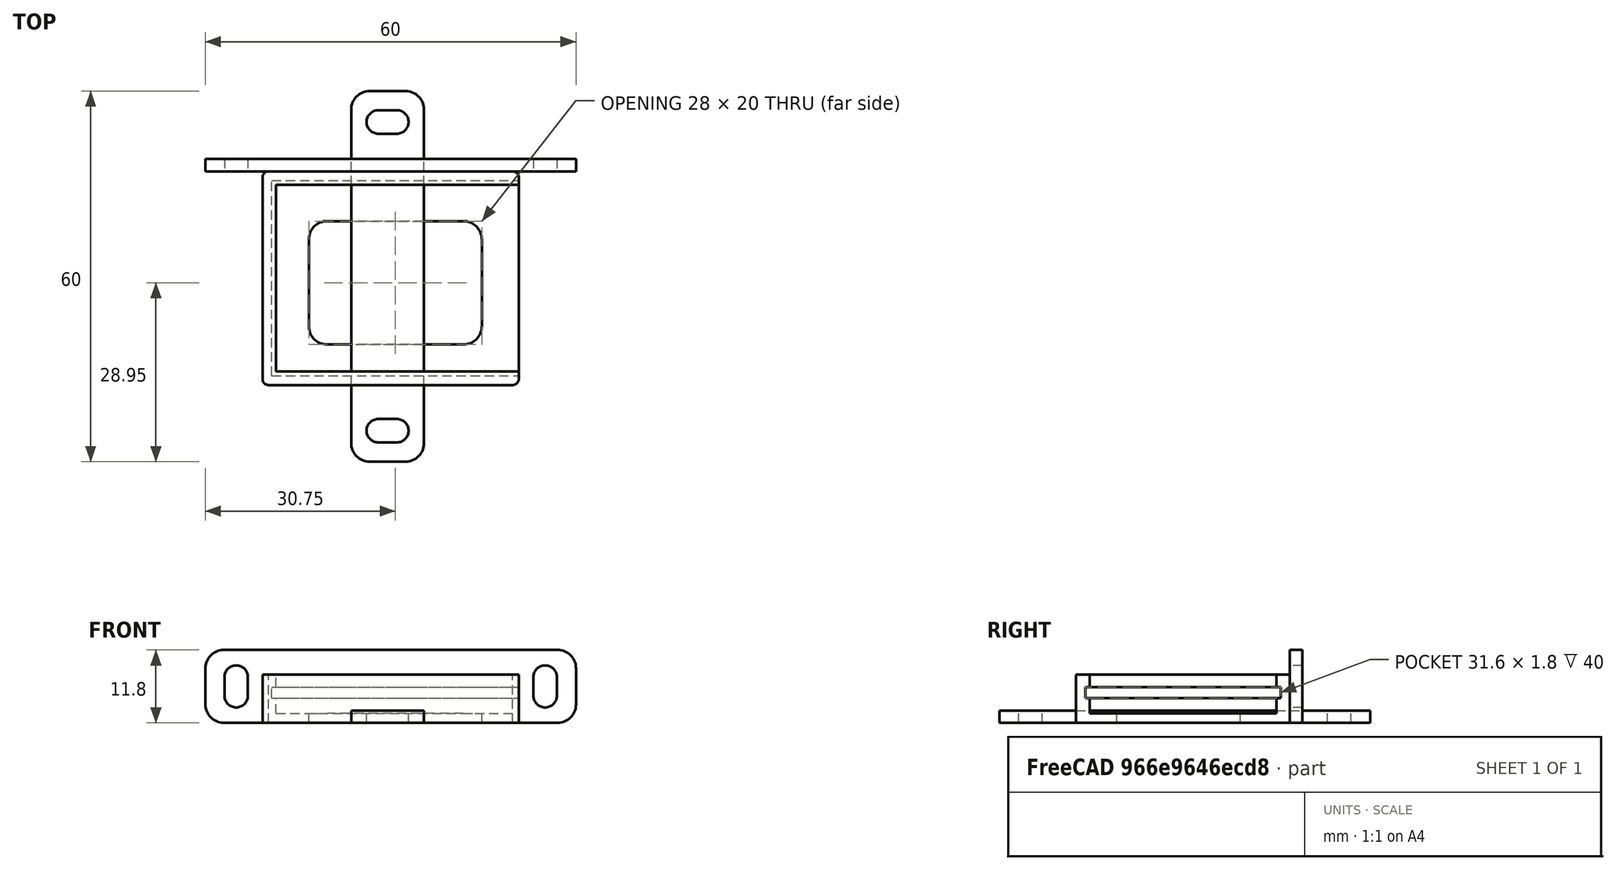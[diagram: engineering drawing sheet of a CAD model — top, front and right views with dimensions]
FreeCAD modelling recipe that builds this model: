
FCSTD DOCUMENT  (FreeCAD 0.19R)
Label: esp32_mini_wroom
License: FreeArt
LicenseURL: http://artlibre.org/licence/lal
objects: Part::Box×4, Part::Fillet×2, Part::MultiFuse×2, Part::Feature×2, Spreadsheet::Sheet×1, Part::Cut×1, App::Part×1
note: 11 computed .brp shape members not serialized (recipe doc carries the construction recipe); baked Part::Feature solids carry a one-line shape summary decoded from their .brp

FEATURE [Spreadsheet::Sheet] Spreadsheet  label="p"
  cells = A1=pcb_x; B1(pcb_x)=40; A2=pcb_y; B2(pcb_y)=31.6; A3=pcb_z; B3(pcb_z)=1.8; A4=pcb_under; B4(pcb_under)=2.5; A5=side_wall; B5(side_wall)=1.5; A6=pcb_side_lane; B6(pcb_side_lane)=0.7; A7=bottom_wall; B7(bottom_wall)=1.5; A8=pcb_above; B8(pcb_above)=2; A9=bottom_hole_x; B9(bottom_hole_x)=28; A10=bottom_hole_y; B10(bottom_hole_y)=20
FEATURE [Part::Box] Box  label="external cube"
  AttacherType = Attacher::AttachEngine3D
  Height = 7.8
  Length = 41.5
  Width = 34.6
  expr: Length = <<p>>.pcb_x + <<p>>.side_wall
  expr: Width = <<p>>.pcb_y + 2 * <<p>>.side_wall
  expr: Height = <<p>>.bottom_wall + <<p>>.pcb_under + <<p>>.pcb_z + <<p>>.pcb_above
FEATURE [Part::Box] Box006  label="internal cube"
  AttacherType = Attacher::AttachEngine3D
  Height = 6.3
  Length = 40.1
  Placement = pos=(2.2,2.2,1.5) rot=(0,0,1;0rad)
  Width = 30.2
  expr: Length = <<p>>.pcb_x - 2 * <<p>>.pcb_side_lane + <<p>>.side_wall
  expr: Width = <<p>>.pcb_y - 2 * <<p>>.pcb_side_lane
  expr: Height = <<p>>.pcb_under + <<p>>.pcb_z + <<p>>.pcb_above
  expr: .Placement.Base.z = <<p>>.bottom_wall
  expr: .Placement.Base.x = <<p>>.side_wall + <<p>>.pcb_side_lane
  expr: .Placement.Base.y = <<p>>.side_wall + <<p>>.pcb_side_lane
FEATURE [Part::Box] Box007  label="pcb extract cube"
  AttacherType = Attacher::AttachEngine3D
  Height = 1.8
  Length = 40
  Placement = pos=(1.5,1.5,4) rot=(0,0,1;0rad)
  Width = 31.6
  expr: Height = <<p>>.pcb_z
  expr: .Placement.Base.z = <<p>>.bottom_wall + <<p>>.pcb_under
  expr: Width = <<p>>.pcb_y
  expr: Length = <<p>>.pcb_x
  expr: .Placement.Base.x = <<p>>.side_wall
  expr: .Placement.Base.y = <<p>>.side_wall
FEATURE [Part::Fillet] Fillet  label="external fillet"
  Base = -> Box
  Edges = 4 edges r=1: [Edge1,Edge3,Edge5,Edge7]
FEATURE [Part::Box] Box008  label="bottom hole"
  AttacherType = Attacher::AttachEngine3D
  Height = 10
  Length = 28
  Placement = pos=(7.5,6.55,0) rot=(0,0,1;0rad)
  Width = 20
  expr: .Placement.Base.y = (<<p>>.pcb_y + <<p>>.side_wall - <<p>>.bottom_hole_y) / 2
  expr: .Placement.Base.x = (<<p>>.pcb_x + 2 * <<p>>.side_wall - <<p>>.bottom_hole_x) / 2
  expr: Width = <<p>>.bottom_hole_y
  expr: Length = <<p>>.bottom_hole_x
FEATURE [Part::Fillet] Fillet001  label="bottom hole fillet"
  Base = -> Box008
  Edges = 4 edges r=3: [Edge1,Edge3,Edge5,Edge7]
FEATURE [Part::MultiFuse] Fusion  label="extract fusion"
  Shapes = -> [Box006,Box007,Fillet001]
FEATURE [Part::Feature] Cut002002  label="attach plane y dir002"
  Placement = pos=(14.35,-12.4,0) rot=(0,0,1;0rad)
  shape: bbox 11.8 x 60 x 2 mm, 20 faces (baked)
FEATURE [Part::Feature] Body002002  label="attach plane x reverse rotated dir002"
  Placement = pos=(-9.25,36.6,0) rot=(1,0,0;1.5708rad)
  shape: bbox 60 x 2 x 11.8 mm, 18 faces (baked)
FEATURE [Part::MultiFuse] Fusion001  label="solid fusion"
  Shapes = -> [Fillet,Body002002]
FEATURE [Part::Cut] Cut  label="body cut"
  Base = -> Fusion001
  Tool = -> Fusion
FEATURE [App::Part] Part  label="esp32 mini wroom pcb box part"
  Group = -> [Box,Fillet,Fusion001,Fusion,Box007,Box006,Cut]
  Origin = -> Origin
